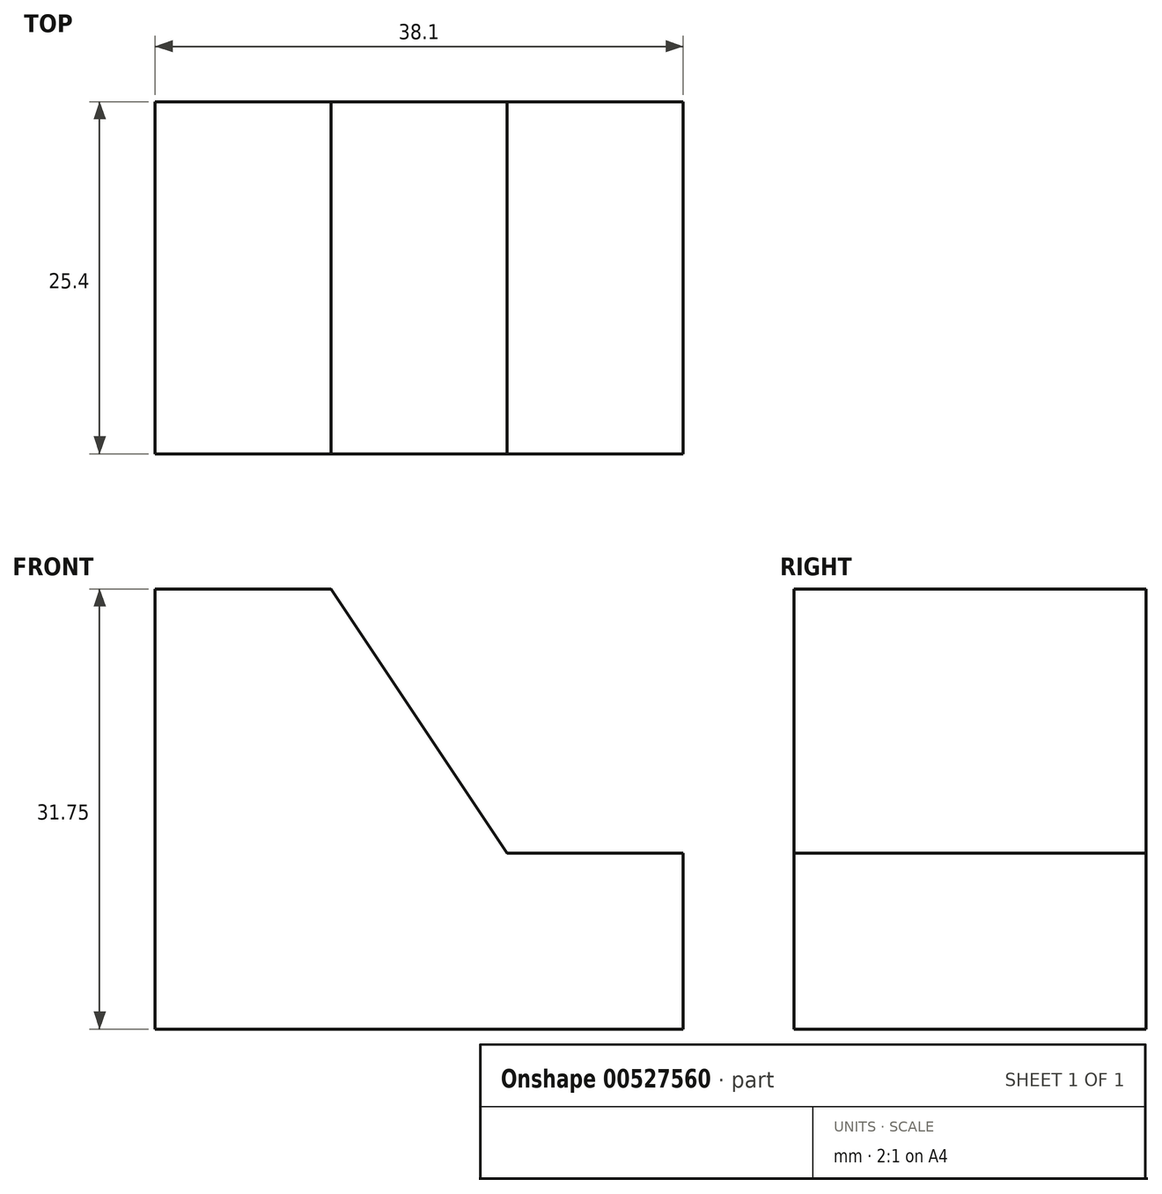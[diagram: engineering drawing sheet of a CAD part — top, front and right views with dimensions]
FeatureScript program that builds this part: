
annotation { "Feature Type Name" : "Feature", "Feature Type Description" : "" }
export const myFeature = defineFeature(function(context is Context, id is Id, definition is map)
    precondition{}
    {
        {
            var Q0;
            Q0=qCreatedBy(makeId("Front.planeOp"),FACE);
            var sketch = newSketch(context, id + "F0", { "sketchPlane" : qUnion([Q0])});
            skLineSegment(sketch, "E0", {"start": v(0, 0) * mm, "end": v(0, 31.75) * mm});
            skLineSegment(sketch, "E1", {"start": v(0, 31.75) * mm, "end": v(38.1, 31.75) * mm});
            skLineSegment(sketch, "E2", {"start": v(38.1, 31.75) * mm, "end": v(38.1, 0) * mm});
            skLineSegment(sketch, "E3", {"start": v(38.1, 0) * mm, "end": v(0, 0) * mm});
            skSolve(sketch);
        }
        {
            var Q0;
            Q0 = qSketchRegion(id + "F0", true);
            extrude(context, id + "F1", {"entities" : qUnion([Q0]), "depth" : 25.4 * mm, "offsetDistance" : 25.4 * mm});
        }
        {
            var Q0;
            Q0=makeQuery(id+"F1.opExtrude","CAP_FACE",FACE,{"disambiguationData":[OSD([sQuery(id+"F0.wireOp",EDGE,"E0"),sQuery(id+"F0.wireOp",EDGE,"E1"),sQuery(id+"F0.wireOp",EDGE,"E2"),sQuery(id+"F0.wireOp",EDGE,"E3")])],"isStart":false});
            var sketch = newSketch(context, id + "F2", { "sketchPlane" : qUnion([Q0])});
            skLineSegment(sketch, "E4", {"start": v(12.7, 31.75) * mm, "end": v(38.1, 31.75) * mm});
            skLineSegment(sketch, "E5", {"start": v(38.1, 31.75) * mm, "end": v(38.1, 12.7) * mm});
            skLineSegment(sketch, "E6", {"start": v(38.1, 12.7) * mm, "end": v(25.4, 12.7) * mm});
            skLineSegment(sketch, "E7", {"start": v(25.4, 12.7) * mm, "end": v(12.7, 31.75) * mm});
            skSolve(sketch);
        }
        {
            var Q0;
            Q0 = qSketchRegion(id + "F2", true);
            extrude(context, id + "F3", {"entities" : qUnion([Q0]), "operationType" : NewBodyOperationType.REMOVE, "oppositeDirection" : true, "depth" : 25.4 * mm, "offsetDistance" : 25.4 * mm});
        }
    });
